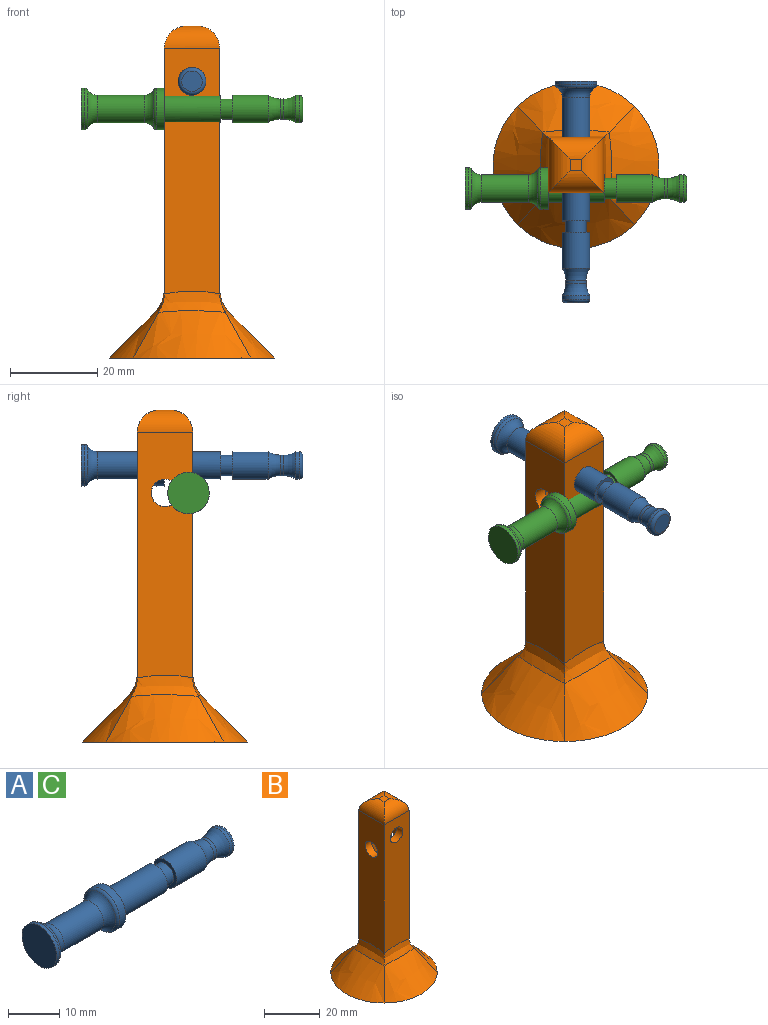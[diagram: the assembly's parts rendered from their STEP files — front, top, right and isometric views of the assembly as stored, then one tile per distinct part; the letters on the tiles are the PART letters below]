
ASSEMBLY  parts=3 mates=1
PART A: 20 faces, bbox 50.8x12.4x12.4 mm
  f0: cylinder r=3.17mm len=13.01mm, axis (-1,0,0), area 259.4mm2, adj f3,f12
  f1: cylinder r=3.17mm len=10.83mm, axis (-1,0,0), area 216.1mm2, adj f8,f9
  f2: cylinder r=4.76mm len=9.53mm, axis (1,0,0), area 51.7mm2, adj f3,f7
  f3: plane 9.53x9.53mm, normal (1,0,0), area 39.6mm2, adj f0,f2
  f4: cylinder r=4.76mm len=9.53mm, axis (-1,0,0), area 23.6mm2, adj f5,f6
  f5: plane 9.53x9.53mm, normal (-1,0,0), area 71.3mm2, adj f4
  f6: torus R=3.95mm, axis (-1,0,0), area 24mm2, adj f4,f8
  f7: torus R=3.95mm, axis (-1,0,0), area 24mm2, adj f2,f9
  f8: torus R=5.71mm, axis (-1,0,0), area 58.2mm2, adj f1,f6
  f9: torus R=5.71mm, axis (-1,0,0), area 58.2mm2, adj f1,f7
  f10: cylinder r=2.36mm len=4.72mm, axis (1,0,0), area 37.7mm2, adj f11,f12
  f11: plane 6.35x6.35mm, normal (-1,0,0), area 14.1mm2, adj f10,f13
  f12: plane 6.35x6.35mm, normal (1,0,0), area 14.1mm2, adj f0,f10
  f13: cylinder r=3.17mm len=8.26mm, axis (-1,0,0), area 164.7mm2, adj f11,f17
  f14: cylinder r=2.36mm len=4.72mm, axis (1,0,0), area 12.4mm2, adj f17,f18
  f15: plane 4.72x4.72mm, normal (1,0,0), area 17.5mm2, adj f19
  f16: cylinder r=3.17mm len=6.35mm, axis (-1,0,0), area 15.7mm2, adj f18,f19
  f17: torus R=7.44mm, axis (-1,0,0), area 48.3mm2, adj f13,f14
  f18: torus R=7.44mm, axis (1,0,0), area 48.3mm2, adj f14,f16
  f19: torus R=2.36mm, axis (1,0,0), area 23.1mm2, adj f15,f16
PART B: 39 faces, bbox 44.5x44.5x82.5 mm
  f0: plane 45.93x6.52mm, normal (1,0,0), area 274.5mm2, adj f18,f20,f23,f34
  f1: plane 45.93x6.52mm, normal (-1,0,0), area 274.5mm2, adj f18,f20,f25,f33
  f2: plane 7.62x6.35mm, normal (0,-1,0), area 32.6mm2, adj f19,f21,f27,f32
  f3: plane 7.62x6.35mm, normal (0,1,0), area 32.6mm2, adj f19,f21,f30,f31
  f4: plane 56.38x12.71mm, normal (0,1,0), area 679.2mm2, adj f5,f7,f14,f32,f35
  f5: plane 56.38x12.71mm, normal (-1,0,0), area 679.2mm2, adj f4,f6,f15,f34,f36
  f6: plane 56.38x12.71mm, normal (0,-1,0), area 679.2mm2, adj f5,f7,f17,f31,f38
  f7: plane 56.38x12.71mm, normal (1,0,0), area 679.2mm2, adj f4,f6,f16,f33,f37
  f8: plane 2.54x2.54mm, normal (0,0,1), area 6.5mm2, adj f14,f15,f16,f17
  f9: plane 38.86x38.86mm, normal (0,0,-1), area 459.8mm2, adj f10,f11,f12,f13,f23,f24,f25,f26
  f10: bspline ~26.94x12.7mm, area 318.9mm2, adj f9,f11,f13,f36
  f11: bspline ~26.94x12.7mm, area 318.9mm2, adj f9,f10,f12,f38
  f12: bspline ~26.94x12.7mm, area 318.8mm2, adj f9,f11,f13,f37
  f13: bspline ~26.94x12.7mm, area 318.8mm2, adj f9,f10,f12,f35
  f14: cylinder r=5.08mm len=12.7mm, axis (-1,0,0), area 60.8mm2, adj f4,f8,f15,f16
  f15: cylinder r=5.08mm len=12.7mm, axis (0,-1,0), area 60.8mm2, adj f5,f8,f14,f17
  f16: cylinder r=5.08mm len=12.7mm, axis (0,1,0), area 60.8mm2, adj f7,f8,f14,f17
  f17: cylinder r=5.08mm len=12.7mm, axis (1,0,0), area 60.8mm2, adj f6,f8,f15,f16
  f18: plane 52.28x6.52mm, normal (0,-1,0), area 314.8mm2, adj f0,f1,f19,f21,f26,f32
  f19: plane 13.97x6.35mm, normal (1,0,0), area 72.9mm2, adj f2,f3,f18,f20,f28,f34
  f20: plane 52.28x6.52mm, normal (0,1,0), area 314.8mm2, adj f0,f1,f19,f21,f24,f31
  f21: plane 13.97x6.35mm, normal (-1,0,0), area 72.9mm2, adj f2,f3,f18,f20,f29,f33
  f22: plane 2.54x2.54mm, normal (0,0,-1), area 6.5mm2, adj f27,f28,f29,f30
  f23: offset ~33.29x20.05mm, area 215.9mm2, adj f0,f9,f24,f26
  f24: offset ~33.29x20.05mm, area 215.9mm2, adj f9,f20,f23,f25
  f25: offset ~33.29x20.05mm, area 215.9mm2, adj f1,f9,f24,f26
  f26: offset ~33.29x20.05mm, area 215.9mm2, adj f9,f18,f23,f25
  f27: cylinder r=1.91mm len=6.35mm, axis (-1,0,0), area 13.3mm2, adj f2,f22,f28,f29
  f28: cylinder r=1.91mm len=6.35mm, axis (0,-1,0), area 13.3mm2, adj f19,f22,f27,f30
  f29: cylinder r=1.91mm len=6.35mm, axis (0,1,0), area 13.3mm2, adj f21,f22,f27,f30
  f30: cylinder r=1.91mm len=6.35mm, axis (1,0,0), area 13.3mm2, adj f3,f22,f28,f29
  f31: cylinder r=3.17mm len=6.35mm, axis (0,-1,0), area 63.3mm2, adj f3,f6,f20
  f32: cylinder r=3.17mm len=6.35mm, axis (0,-1,0), area 63.3mm2, adj f2,f4,f18
  f33: cylinder r=3.17mm len=6.35mm, axis (-1,0,0), area 63.3mm2, adj f1,f7,f21
  f34: cylinder r=3.17mm len=6.35mm, axis (-1,0,0), area 63.3mm2, adj f0,f5,f19
  f35: bspline ~18.35x4.97mm, area 67.5mm2, adj f4,f13,f36,f37
  f36: bspline ~18.66x4.99mm, area 67.7mm2, adj f5,f10,f35,f38
  f37: bspline ~18.35x4.97mm, area 67.5mm2, adj f7,f12,f35,f38
  f38: bspline ~18.66x4.99mm, area 67.7mm2, adj f6,f11,f36,f37
PART C: same geometry as A
PLACE A rot(axis=(0,0,-1),90deg) t=(0,-0.8,6.35)mm
PLACE B t=(0,5.4,0)mm
PLACE C at identity
MATE pin_slot A.f0 <-> B.f31  axis (0,1,0) through (0,-0.95,63.5)mm
